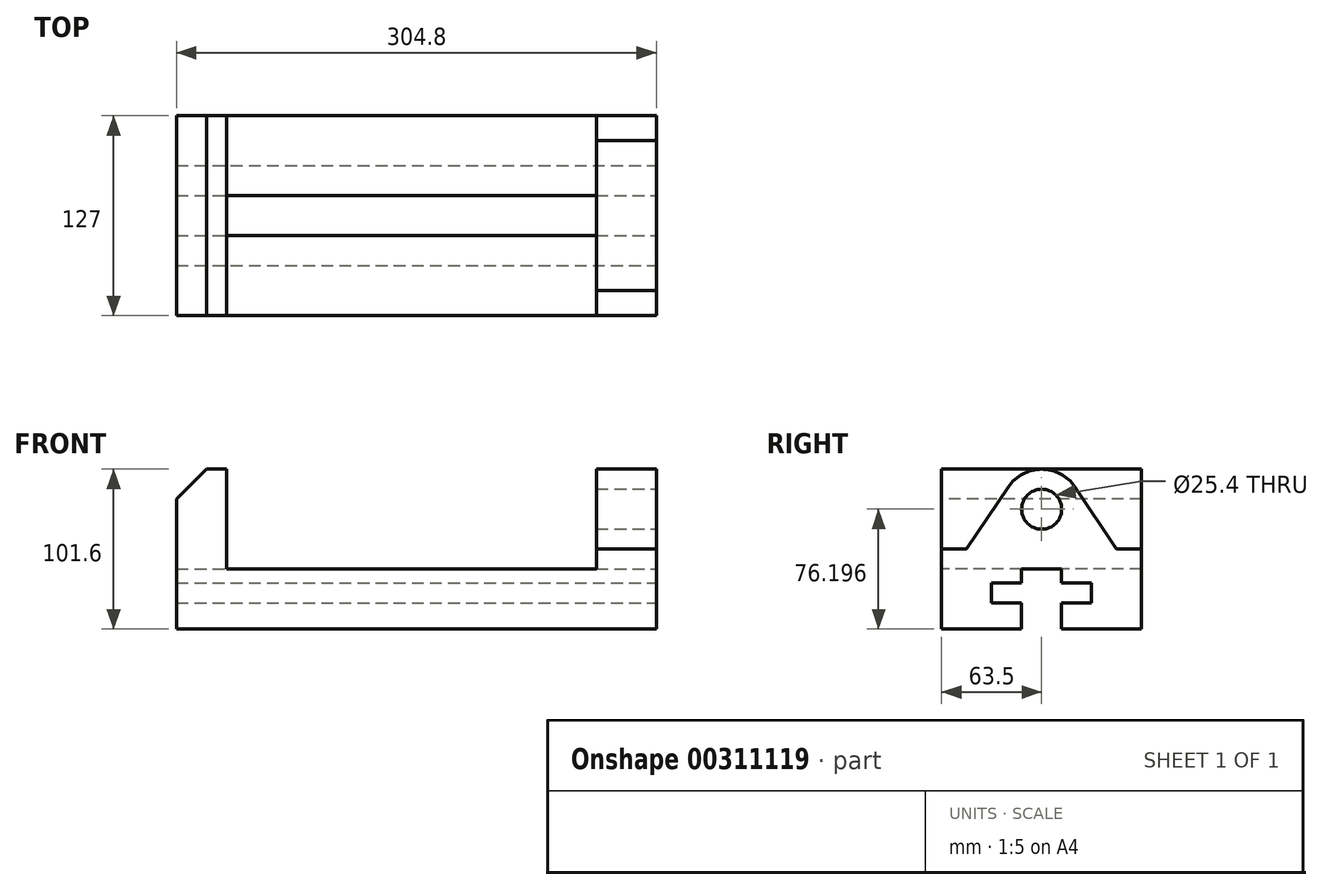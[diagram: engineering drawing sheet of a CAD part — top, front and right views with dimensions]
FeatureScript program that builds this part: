
annotation { "Feature Type Name" : "Feature", "Feature Type Description" : "" }
export const myFeature = defineFeature(function(context is Context, id is Id, definition is map)
    precondition{}
    {
        {
            var Q0;
            Q0=qCreatedBy(makeId("Front.planeOp"),FACE);
            var sketch = newSketch(context, id + "F0", { "sketchPlane" : qUnion([Q0])});
            skLineSegment(sketch, "E0", {"start": v(-27.68, 28.56) * mm, "end": v(-59.43, 28.56) * mm});
            skLineSegment(sketch, "E1", {"start": v(-59.43, 28.56) * mm, "end": v(-59.43, -73.04) * mm});
            skLineSegment(sketch, "E2", {"start": v(-59.43, -73.04) * mm, "end": v(245.37, -73.04) * mm});
            skLineSegment(sketch, "E3", {"start": v(245.37, -73.04) * mm, "end": v(245.37, 28.56) * mm});
            skLineSegment(sketch, "E4", {"start": v(245.37, 28.56) * mm, "end": v(207.27, 28.56) * mm});
            skLineSegment(sketch, "E5", {"start": v(207.27, 28.56) * mm, "end": v(207.27, -34.94) * mm});
            skLineSegment(sketch, "E6", {"start": v(207.27, -34.94) * mm, "end": v(-27.68, -34.94) * mm});
            skLineSegment(sketch, "E7", {"start": v(-27.68, -34.94) * mm, "end": v(-27.68, 28.56) * mm});
            skSolve(sketch);
        }
        {
            var Q0;
            Q0 = qSketchRegion(id + "F0", true);
            extrude(context, id + "F1", {"entities" : qUnion([Q0]), "oppositeDirection" : true, "depth" : 127 * mm});
        }
        {
            var Q0;
            Q0=makeQuery(id+"F1.opExtrude","CAP_FACE",FACE,{"disambiguationData":[OSD([sQuery(id+"F0.wireOp",EDGE,"E0"),sQuery(id+"F0.wireOp",EDGE,"E1"),sQuery(id+"F0.wireOp",EDGE,"E2"),sQuery(id+"F0.wireOp",EDGE,"E3"),sQuery(id+"F0.wireOp",EDGE,"E4"),sQuery(id+"F0.wireOp",EDGE,"E5"),sQuery(id+"F0.wireOp",EDGE,"E6"),sQuery(id+"F0.wireOp",EDGE,"E7")])],"isStart":true});
            var sketch = newSketch(context, id + "F2", { "sketchPlane" : qUnion([Q0])});
            skLineSegment(sketch, "E8", {"start": v(-59.43, 28.56) * mm, "end": v(-40.38, 28.56) * mm});
            skLineSegment(sketch, "E9", {"start": v(-59.43, 28.56) * mm, "end": v(-59.43, 9.5) * mm});
            skLineSegment(sketch, "E10", {"start": v(-59.43, 9.5) * mm, "end": v(-40.38, 28.56) * mm});
            skSolve(sketch);
        }
        {
            var Q0;
            Q0 = qSketchRegion(id + "F2", true);
            extrude(context, id + "F3", {"entities" : qUnion([Q0]), "operationType" : NewBodyOperationType.REMOVE, "oppositeDirection" : true, "depth" : 127 * mm});
        }
        {
            var Q0;
            Q0=makeQuery(id+"F1.opExtrude","SWEPT_FACE",FACE,{"disambiguationData":[OSD([sQuery(id+"F0.wireOp",EDGE,"E3")])]});
            var sketch = newSketch(context, id + "F4", { "sketchPlane" : qUnion([Q0])});
            skLineSegment(sketch, "E11", {"start": v(63.5, -73.04) * mm, "end": v(76.2, -73.04) * mm});
            skLineSegment(sketch, "E12", {"start": v(76.2, -73.04) * mm, "end": v(76.2, -56.53) * mm});
            skLineSegment(sketch, "E13", {"start": v(76.2, -56.53) * mm, "end": v(95.25, -56.53) * mm});
            skLineSegment(sketch, "E14", {"start": v(95.25, -56.53) * mm, "end": v(95.25, -43.83) * mm});
            skLineSegment(sketch, "E15", {"start": v(95.25, -43.83) * mm, "end": v(76.2, -43.83) * mm});
            skLineSegment(sketch, "E16", {"start": v(76.2, -43.83) * mm, "end": v(76.2, -34.94) * mm});
            skLineSegment(sketch, "E17", {"start": v(76.2, -34.94) * mm, "end": v(50.8, -34.94) * mm});
            skLineSegment(sketch, "E18", {"start": v(50.8, -34.94) * mm, "end": v(50.8, -43.83) * mm});
            skLineSegment(sketch, "E19", {"start": v(50.8, -43.83) * mm, "end": v(31.75, -43.83) * mm});
            skLineSegment(sketch, "E20", {"start": v(31.75, -43.83) * mm, "end": v(31.75, -56.53) * mm});
            skLineSegment(sketch, "E21", {"start": v(31.75, -56.53) * mm, "end": v(50.8, -56.53) * mm});
            skLineSegment(sketch, "E22", {"start": v(50.8, -56.53) * mm, "end": v(50.8, -73.04) * mm});
            skLineSegment(sketch, "E23", {"start": v(50.8, -73.04) * mm, "end": v(63.5, -73.04) * mm});
            skSolve(sketch);
        }
        {
            var Q0;
            Q0 = qSketchRegion(id + "F4", true);
            extrude(context, id + "F5", {"entities" : qUnion([Q0]), "operationType" : NewBodyOperationType.REMOVE, "endBound" : BoundingType.THROUGH_ALL, "oppositeDirection" : true, "depth" : 25.4 * mm});
        }
        {
            var Q0;
            Q0=makeQuery(id+"F1.opExtrude","SWEPT_FACE",FACE,{"disambiguationData":[OSD([sQuery(id+"F0.wireOp",EDGE,"E3")])]});
            var sketch = newSketch(context, id + "F6", { "sketchPlane" : qUnion([Q0])});
            skLineSegment(sketch, "E24", {"start": v(0, -22.24) * mm, "end": v(15.88, -22.24) * mm});
            skLineSegment(sketch, "E25", {"start": v(15.88, -22.24) * mm, "end": v(42.4, 17.3) * mm});
            skArc(sketch, "E26", {"start": v(84.6, 17.3) * mm, "mid": v(63.5, 28.56) * mm, "end": v(42.4, 17.3) * mm});
            skLineSegment(sketch, "E27", {"start": v(84.6, 17.3) * mm, "end": v(111.12, -22.24) * mm});
            skLineSegment(sketch, "E28", {"start": v(111.12, -22.24) * mm, "end": v(127, -22.24) * mm});
            skSolve(sketch);
        }
        {
            var Q0;
            Q0 = qSketchRegion(id + "F6", true);
            var Q1;
            {var subQ7=sQuery(id+"F6.wireOp",EDGE,"E24");Q1=makeQuery(id+"F6.imprint","IMPRINT",FACE,{"disambiguationData":[TD([[makeQuery(id+"F6.imprint","IMPRINT",EDGE,{"derivedFrom":subQ7}),1.0]])]});}
            var Q2;
            {var subQ7=sQuery(id+"F6.wireOp",EDGE,"E27");Q2=makeQuery(id+"F6.imprint","IMPRINT",FACE,{"disambiguationData":[TD([[makeQuery(id+"F6.imprint","IMPRINT",EDGE,{"derivedFrom":subQ7}),1.0]])]});}
            extrude(context, id + "F7", {"entities" : qUnion([Q0, Q1, Q2]), "operationType" : NewBodyOperationType.REMOVE, "oppositeDirection" : true, "depth" : 38.1 * mm});
        }
        {
            var Q0;
            Q0=makeQuery(id+"F1.opExtrude","SWEPT_FACE",FACE,{"disambiguationData":[OSD([sQuery(id+"F0.wireOp",EDGE,"E3")])]});
            var sketch = newSketch(context, id + "F8", { "sketchPlane" : qUnion([Q0])});
            skCircle(sketch, "E29", {"center": v(63.5, 3.16) * mm, "radius": 12.7 * mm});
            skSolve(sketch);
        }
        {
            var Q0;
            Q0 = qSketchRegion(id + "F8", true);
            extrude(context, id + "F9", {"entities" : qUnion([Q0]), "operationType" : NewBodyOperationType.REMOVE, "oppositeDirection" : true, "depth" : 38.1 * mm});
        }
    });
